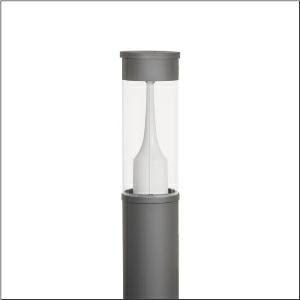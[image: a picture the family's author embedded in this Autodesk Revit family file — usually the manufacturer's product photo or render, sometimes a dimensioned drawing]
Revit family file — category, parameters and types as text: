
# Revit family: city-light_260_iq___p1_0a_5xa5295lf14h_3d8e
name_source: partatom
category: Lighting Fixtures
units: mm (PartAtom-declared; Revit-internal decimal feet)

## family parameters
Cut with Voids When Loaded = No
Host = Face
Light Source = No
Part Type = Normal
Room Calculation Point = No
Round Connector Dimension = Use Diameter
Shared = No

## types (1)
- --- (1 x LED, 1510 lm, 10 W, 4000K)
    Apparent Load = 10 VA
    CIE Flux Codes = 32 61 90 93 100
    Color Rendering = 70
    Color Temperature = 4000K
    Default Elevation = 1800 mm
    Description = City-Light 260 iQ, light pillar, Module 540 iQ-SR, primary light control with 3 zone facetted reflector, of plastic, silver coated, highly specular, structured, primary optical cover: cover, of PMMA, transparent, partly coated, light distribution: P1.0a, primary light characteristic: strongly asymmetric, LED, High Power LED, rated luminous flux: 1.510lm, luminous efficacy: 151lm/W, light colour: 740, colour temperature: 4000K, control gear: ECG iQ, control: presetting dimming logarithmic, Street-Remote, Auto-Match, Temp-Guard, Lumen-Switch, Night-Set, Smart-Wire, Light-Fading, Desk-Remote (wireless, voltage-free reading and setting of iQ features in the workshop via application-optimized NFC function/RFID function), optimised constant luminous flux control (CLO 2.0), with terminal, 6-pole, max. 2.5mm², mains connection: 230..240V, AC, 50/60Hz, start of lifetime: 10W, end of service life: 10W, reduction: 5W, luminaire housing, cylindrical, of extruded aluminium section, coated, Siteco® metallic grey (DB 702S), length: 2.600mm, diameter: 200mm, Module 540 iQ-SR, traffic white (RAL 9016), equipment: standard, protection rating (complete): IP65, insulation class (complete): insulation class II (safety insulation), certification: CE, ENEC, VDE, packaging unit: 1 piece

Light Distribution: P1.0a
    Height = 500 mm
    Lamp = 1 x LED
    Lamp Light Flux = 1510 lm
    Lamp Power = 10 W
    Lamp count = 1
    Length = 200 mm  [stored 0.656168 ft]
    Luminous efficacy = 151 lm/W
    Manufacturer = Siteco
    ModVariant = No
    Model = 5XA5295LF14H
    Mounting Place = Floor
    Mounting Type = Freestanding
    Number of Poles = 1
    OnlyDefault = Yes
    Power Factor = 1
    Product Name = City-Light 260 iQ | P1.0a
    Product group = light pillar
    ProductGroupID = 1303
    Protection Class = Protection class II
    Protection Degree = IP 65
    RLX_Detail_Level = 1
    RLX_Emergency_Light_Flux = 0 lm
    RLX_Emergency_Type = 0
    RLX_Emergency_Type_DB = No
    RlxData = <blob elided: 57041 chars, md5=91a97592>
    Socket = socket
    Standby Power = 0 W
    System Light Flux = 1510 lm
    System Power = 10 W
    Type Comments = factory setting: luminous flux: 100 % | dim-lin: 254 | 401 mA
    Type Image = l_1006918.jpg
    URL = http://relux.com
    VarID = @adj_091789
    Voltage = 0 V
    Weight = 0.00 kg
    Width = 0 mm  [stored 0 ft]

note: [stored X ft] marks values corroborated as IEEE doubles in the binary element streams (Revit-internal decimal feet)

## geometry (parser evidence)
native form markers: Blend x4, Sweep x11
no freeform markers — native parametric forms only
